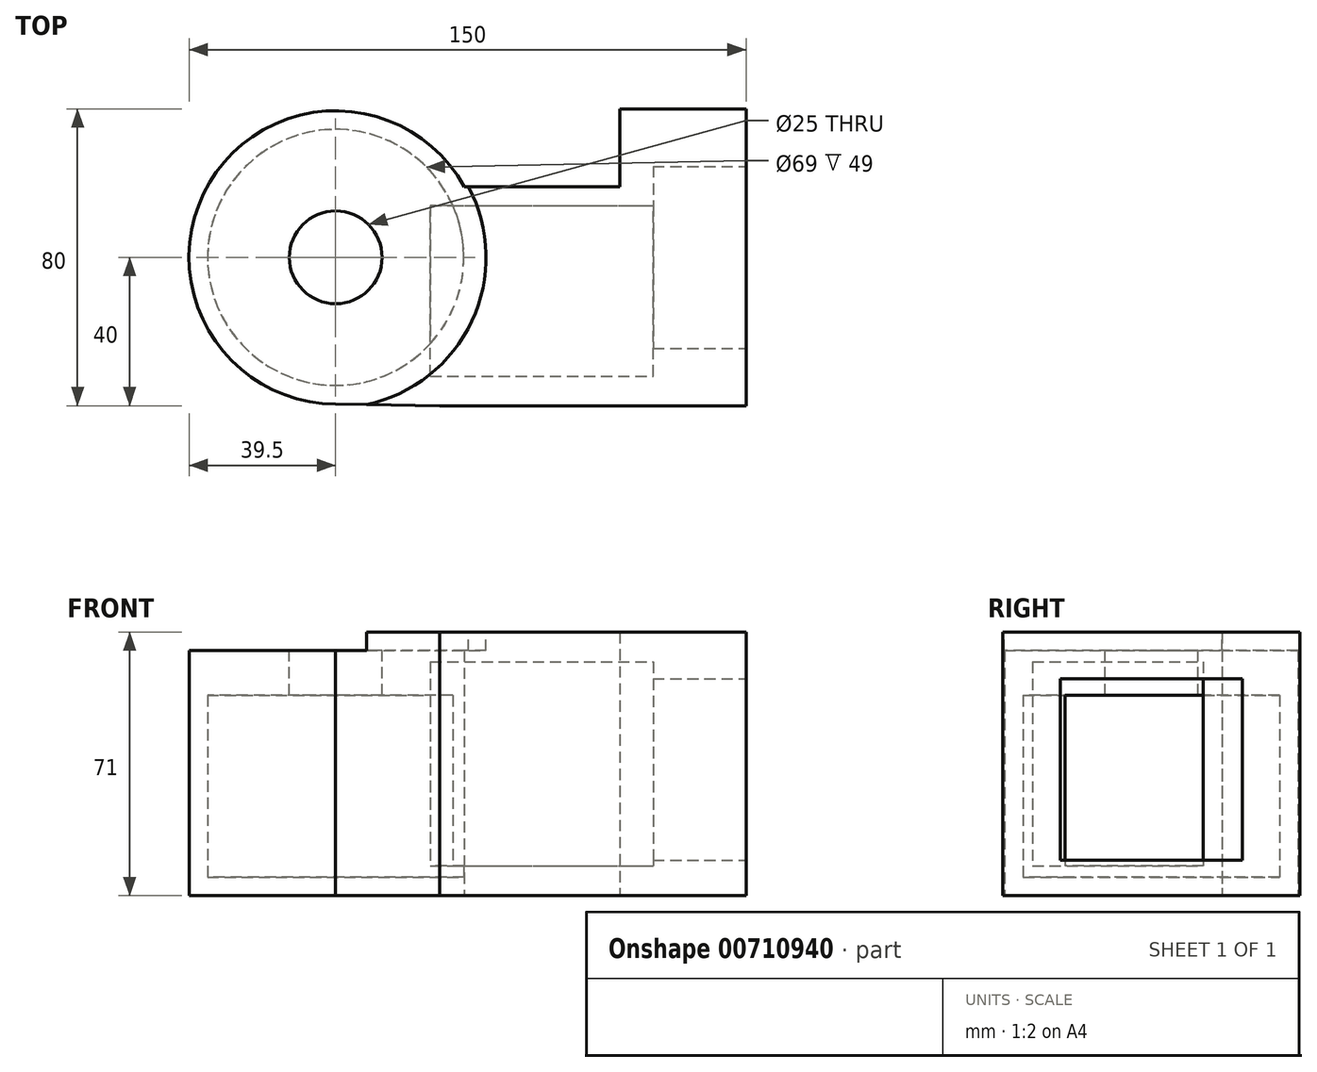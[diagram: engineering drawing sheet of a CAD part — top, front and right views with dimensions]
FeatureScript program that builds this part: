
annotation { "Feature Type Name" : "Feature", "Feature Type Description" : "" }
export const myFeature = defineFeature(function(context is Context, id is Id, definition is map)
    precondition{}
    {
        {
            var Q0;
            Q0=qCreatedBy(makeId("Top.planeOp"),FACE);
            var sketch = newSketch(context, id + "F0", { "sketchPlane" : qUnion([Q0])});
            skCircle(sketch, "E0", {"center": v(-35.5, 40) * mm, "radius": 39.5 * mm});
            skPoint(sketch, "E1.middle", {"position": v(0, 0) * mm});
            skLineSegment(sketch, "E2", {"start": v(75, 0) * mm, "end": v(75, 80) * mm});
            skLineSegment(sketch, "E3", {"start": v(75, 80) * mm, "end": v(41, 80) * mm});
            skLineSegment(sketch, "E4", {"start": v(41, 80) * mm, "end": v(41, 59) * mm});
            skLineSegment(sketch, "E5", {"start": v(41, 59) * mm, "end": v(-0.87, 59) * mm});
            skLineSegment(sketch, "E6", {"start": v(75, 0) * mm, "end": v(-7.5, 0) * mm});
            skLineSegment(sketch, "E7", {"start": v(-7.5, 0) * mm, "end": v(-35.5, 0.5) * mm});
            skSolve(sketch);
        }
        {
            var Q0;
            {var subQ0=sQuery(id+"F0.wireOp",EDGE,"E0");var subQ1=makeQuery(id+"F0.imprint","INTERSECT",VERTEX,{"derivedFrom":[subQ0,sQuery(id+"F0.wireOp",EDGE,"E5")]});Q0=makeQuery(id+"F0.imprint","IMPRINT",FACE,{"disambiguationData":[TD([[makeQuery(id+"F0.imprint","IMPRINT",EDGE,{"disambiguationData":[TD([[subQ1,-1.0]])],"derivedFrom":subQ0}),1.0]])]});}
            var Q1;
            Q1=makeQuery(id+"F0.imprint","IMPRINT",FACE,{"disambiguationData":[TD([[makeQuery(id+"F0.imprint","IMPRINT",EDGE,{"derivedFrom":sQuery(id+"F0.wireOp",EDGE,"E2")}),1.0]])]});
            extrude(context, id + "F1", {"entities" : qUnion([Q0, Q1]), "depth" : 71 * mm, "offsetDistance" : 25 * mm});
        }
        {
            var Q0;
            Q0=makeQuery(id+"F1.opExtrude","SWEPT_FACE",FACE,{"disambiguationData":[OSD([sQuery(id+"F0.wireOp",EDGE,"E2")])]});
            var sketch = newSketch(context, id + "F2", { "sketchPlane" : qUnion([Q0])});
            skLineSegment(sketch, "E8.bottom", {"start": v(64.5, 9.5) * mm, "end": v(15.5, 9.5) * mm});
            skLineSegment(sketch, "E8.top", {"start": v(64.5, 58.5) * mm, "end": v(15.5, 58.5) * mm});
            skLineSegment(sketch, "E8.left", {"start": v(64.5, 9.5) * mm, "end": v(64.5, 58.5) * mm});
            skLineSegment(sketch, "E8.right", {"start": v(15.5, 9.5) * mm, "end": v(15.5, 58.5) * mm});
            skPoint(sketch, "E8.middle", {"position": v(40, 34) * mm});
            skSolve(sketch);
        }
        {
            var Q0;
            Q0=makeQuery(id+"F2.imprint","IMPRINT",FACE,{"disambiguationData":[TD([[makeQuery(id+"F2.imprint","IMPRINT",EDGE,{"derivedFrom":sQuery(id+"F2.wireOp",EDGE,"E8.bottom")}),-1.0]])]});
            extrude(context, id + "F3", {"entities" : qUnion([Q0]), "operationType" : NewBodyOperationType.REMOVE, "oppositeDirection" : true, "depth" : 25 * mm, "offsetDistance" : 25 * mm});
        }
        {
            var Q0;
            Q0=qCreatedBy(makeId("Right.planeOp"),FACE);
            cPlane(context, id + "F4", {"entities" : qUnion([Q0]), "cplaneType" : CPlaneType.OFFSET, "offset" : 50 * mm, "width" : 150 * mm, "height" : 150 * mm});
        }
        {
            var Q0;
            Q0=qCreatedBy(id+"F4.planeOp",FACE);
            var sketch = newSketch(context, id + "F5", { "sketchPlane" : qUnion([Q0])});
            skLineSegment(sketch, "E9.bottom", {"start": v(8, 63) * mm, "end": v(54, 63) * mm});
            skLineSegment(sketch, "E9.top", {"start": v(8, 8) * mm, "end": v(54, 8) * mm});
            skLineSegment(sketch, "E9.left", {"start": v(8, 63) * mm, "end": v(8, 8) * mm});
            skLineSegment(sketch, "E9.right", {"start": v(54, 63) * mm, "end": v(54, 8) * mm});
            skSolve(sketch);
        }
        {
            var Q0;
            Q0=makeQuery(id+"F5.imprint","IMPRINT",FACE,{"disambiguationData":[TD([[makeQuery(id+"F5.imprint","IMPRINT",EDGE,{"derivedFrom":sQuery(id+"F5.wireOp",EDGE,"E9.bottom")}),-1.0]])]});
            extrude(context, id + "F6", {"entities" : qUnion([Q0]), "operationType" : NewBodyOperationType.REMOVE, "oppositeDirection" : true, "depth" : 60 * mm, "offsetDistance" : 25 * mm});
        }
        {
            var Q0;
            Q0=qCreatedBy(makeId("Top.planeOp"),FACE);
            cPlane(context, id + "F7", {"entities" : qUnion([Q0]), "cplaneType" : CPlaneType.OFFSET, "offset" : 5 * mm, "width" : 150 * mm, "height" : 150 * mm});
        }
        {
            var Q0;
            Q0=qCreatedBy(id+"F7.planeOp",FACE);
            var sketch = newSketch(context, id + "F8", { "sketchPlane" : qUnion([Q0])});
            skCircle(sketch, "E10", {"center": v(-35.5, 40) * mm, "radius": 34.5 * mm});
            skSolve(sketch);
        }
        {
            var Q0;
            Q0=makeQuery(id+"F8.imprint","IMPRINT",FACE,{"disambiguationData":[TD([[makeQuery(id+"F8.imprint","IMPRINT",EDGE,{"derivedFrom":sQuery(id+"F8.wireOp",EDGE,"E10")}),1.0]])]});
            extrude(context, id + "F9", {"entities" : qUnion([Q0]), "operationType" : NewBodyOperationType.REMOVE, "depth" : 49 * mm, "offsetDistance" : 25 * mm});
        }
        {
            var Q0;
            Q0=makeQuery(id+"F1.opExtrude","CAP_FACE",FACE,{"disambiguationData":[OSD([sQuery(id+"F0.wireOp",EDGE,"E0"),sQuery(id+"F0.wireOp",EDGE,"E2"),sQuery(id+"F0.wireOp",EDGE,"E3"),sQuery(id+"F0.wireOp",EDGE,"E4"),sQuery(id+"F0.wireOp",EDGE,"E5"),sQuery(id+"F0.wireOp",EDGE,"E6"),sQuery(id+"F0.wireOp",EDGE,"E7")])],"isStart":false});
            var sketch = newSketch(context, id + "F10", { "sketchPlane" : qUnion([Q0])});
            skCircle(sketch, "E11", {"center": v(-35.5, 40) * mm, "radius": 12.5 * mm});
            skSolve(sketch);
        }
        {
            var Q0;
            Q0=makeQuery(id+"F10.imprint","IMPRINT",FACE,{"disambiguationData":[TD([[makeQuery(id+"F10.imprint","IMPRINT",EDGE,{"derivedFrom":sQuery(id+"F10.wireOp",EDGE,"E11")}),1.0]])]});
            extrude(context, id + "F11", {"entities" : qUnion([Q0]), "operationType" : NewBodyOperationType.REMOVE, "oppositeDirection" : true, "depth" : 25 * mm, "offsetDistance" : 25 * mm});
        }
        {
            var Q0;
            Q0=makeQuery(id+"F1.opExtrude","CAP_FACE",FACE,{"disambiguationData":[OSD([sQuery(id+"F0.wireOp",EDGE,"E0"),sQuery(id+"F0.wireOp",EDGE,"E2"),sQuery(id+"F0.wireOp",EDGE,"E3"),sQuery(id+"F0.wireOp",EDGE,"E4"),sQuery(id+"F0.wireOp",EDGE,"E5"),sQuery(id+"F0.wireOp",EDGE,"E6"),sQuery(id+"F0.wireOp",EDGE,"E7")])],"isStart":false});
            var sketch = newSketch(context, id + "F12", { "sketchPlane" : qUnion([Q0])});
            skCircle(sketch, "E12", {"center": v(-35.5, 40) * mm, "radius": 40.5 * mm});
            skSolve(sketch);
        }
        {
            var Q0;
            {var subQ1=makeQuery(id+"F1.opExtrude","CAP_EDGE",EDGE,{"disambiguationData":[OSD([sQuery(id+"F0.wireOp",EDGE,"E0")])],"isStart":false});Q0=makeQuery(id+"F12.imprint","IMPRINT",FACE,{"disambiguationData":[TD([[makeQuery(id+"F12.imprint","IMPRINT",EDGE,{"derivedFrom":subQ1}),1.0]])]});}
            var Q1;
            {var subQ5=makeQuery(id+"F1.opExtrude","CAP_EDGE",EDGE,{"disambiguationData":[OSD([sQuery(id+"F0.wireOp",EDGE,"E0")])],"isStart":false});Q1=makeQuery(id+"F12.imprint","IMPRINT",FACE,{"disambiguationData":[TD([[makeQuery(id+"F12.imprint","IMPRINT",EDGE,{"derivedFrom":subQ5}),-1.0]])]});}
            extrude(context, id + "F13", {"entities" : qUnion([Q0, Q1]), "operationType" : NewBodyOperationType.REMOVE, "oppositeDirection" : true, "depth" : 5 * mm, "offsetDistance" : 25 * mm});
        }
    });
